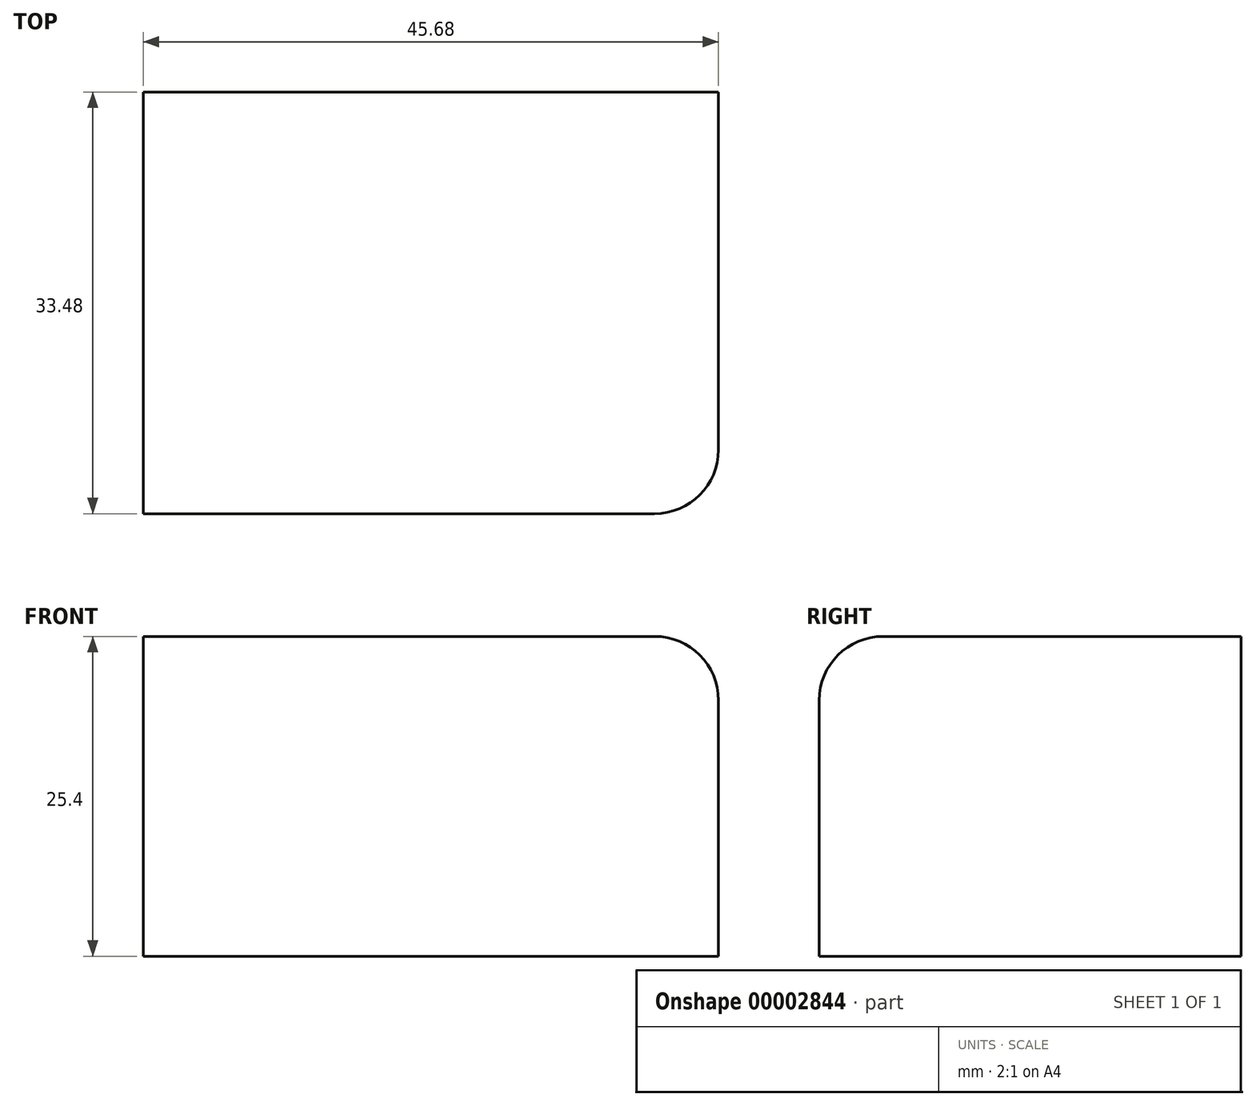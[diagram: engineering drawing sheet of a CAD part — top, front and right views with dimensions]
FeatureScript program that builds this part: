
annotation { "Feature Type Name" : "Feature", "Feature Type Description" : "" }
export const myFeature = defineFeature(function(context is Context, id is Id, definition is map)
    precondition{}
    {
        {
            var Q0;
            Q0=qCreatedBy(makeId("Top.planeOp"),FACE);
            var sketch = newSketch(context, id + "F0", { "sketchPlane" : qUnion([Q0])});
            skLineSegment(sketch, "E0.rect.bottom", {"start": v(22.84, 16.74) * mm, "end": v(-22.84, 16.74) * mm});
            skLineSegment(sketch, "E0.rect.top", {"start": v(22.84, -16.74) * mm, "end": v(-22.84, -16.74) * mm});
            skLineSegment(sketch, "E0.rect.left", {"start": v(22.84, 16.74) * mm, "end": v(22.84, -16.74) * mm});
            skLineSegment(sketch, "E0.rect.right", {"start": v(-22.84, 16.74) * mm, "end": v(-22.84, -16.74) * mm});
            skPoint(sketch, "E0.rect.middle", {"position": v(0, 0) * mm});
            skSolve(sketch);
        }
        {
            var Q0;
            Q0=makeQuery(id+"F0.imprint","IMPRINT",FACE,{"disambiguationData":[TD([[makeQuery(id+"F0.imprint","IMPRINT",EDGE,{"derivedFrom":sQuery(id+"F0.wireOp",EDGE,"E0.rect.bottom")}),1.0]])]});
            extrude(context, id + "F1", {"entities" : qUnion([Q0]), "depth" : 25.4 * mm});
        }
        {
            var Q0;
            Q0=makeQuery(id+"F1.opExtrude","CAP_EDGE",EDGE,{"disambiguationData":[OSD([sQuery(id+"F0.wireOp",EDGE,"E0.rect.top")])],"isStart":false});
            fillet(context, id + "F2", {"entities" : qUnion([Q0]), "radius" : 5.08 * mm, "tangentPropagation" : true, "allowEdgeOverflow" : false});
        }
        {
            var Q0;
            Q0=makeQuery(id+"F1.opExtrude","CAP_EDGE",EDGE,{"disambiguationData":[OSD([sQuery(id+"F0.wireOp",EDGE,"E0.rect.left")])],"isStart":false});
            fillet(context, id + "F3", {"entities" : qUnion([Q0]), "radius" : 5.08 * mm, "tangentPropagation" : true, "allowEdgeOverflow" : false});
        }
    });
